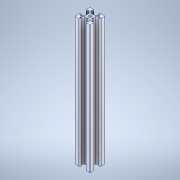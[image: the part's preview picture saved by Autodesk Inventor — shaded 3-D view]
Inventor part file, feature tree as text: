
AUTODESK INVENTOR PART (.ipt)
format: ipt  version: 2021 (Build 250183000, 183)  size: 237,056 bytes
history: native  units: mm
features: sketch x3, extrude x2, fillet x2, other x1, pattern_circular x1, hole x1, projected_geometry x1
ambient origin geometry x8: Origin, YZ Plane, XZ Plane, XY Plane, X Axis, Y Axis, Z Axis, Center Point
bodies: Body1 (feature_tree)
feature tree (11):
  other  "實體1"
  extrude  "擠出1"  Depth=20.0mm
  extrude  "擠出2"  Depth=20.0mm
  fillet  "圓角1"  Radius=170.0mm
  pattern_circular  "環形陣列1"  [2 undecoded]
  hole  "孔1"  [1 undecoded]
  fillet  "圓角2"  Radius=6.2mm
  sketch  "草圖1"
  sketch  "草圖2"
  projected_geometry  "投影迴路1"
  sketch  "草圖3"
note: 3 required parameter values undecoded (feature->parameter linkage not recoverable at this tier; creation-order binding heuristic only, values carry confidence <= 0.55)
